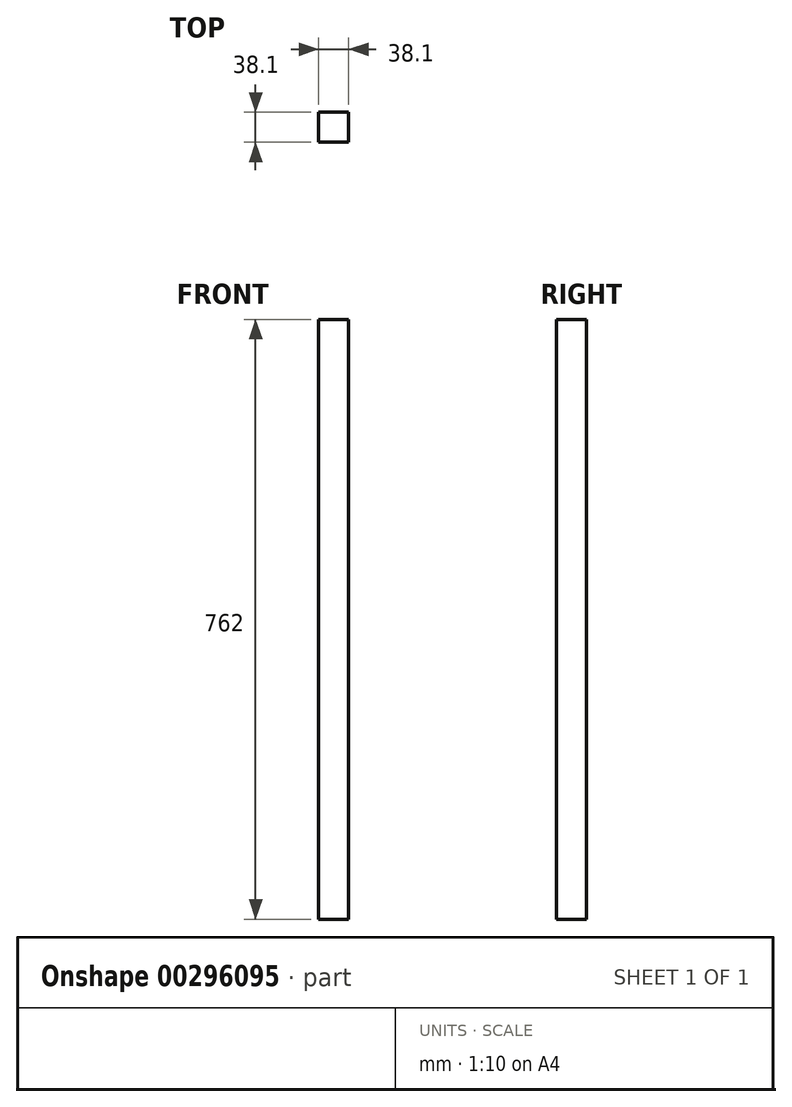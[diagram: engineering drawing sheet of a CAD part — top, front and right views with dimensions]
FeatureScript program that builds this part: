
annotation { "Feature Type Name" : "Feature", "Feature Type Description" : "" }
export const myFeature = defineFeature(function(context is Context, id is Id, definition is map)
    precondition{}
    {
        {
            var Q0;
            Q0=qCreatedBy(makeId("Front.planeOp"),FACE);
            var sketch = newSketch(context, id + "F0", { "sketchPlane" : qUnion([Q0])});
            skLineSegment(sketch, "E0.bottom", {"start": v(19.05, 381) * mm, "end": v(-19.05, 381) * mm});
            skLineSegment(sketch, "E0.top", {"start": v(19.05, -381) * mm, "end": v(-19.05, -381) * mm});
            skLineSegment(sketch, "E0.left", {"start": v(19.05, 381) * mm, "end": v(19.05, -381) * mm});
            skLineSegment(sketch, "E0.right", {"start": v(-19.05, 381) * mm, "end": v(-19.05, -381) * mm});
            skPoint(sketch, "E0.middle", {"position": v(0, 0) * mm});
            skSolve(sketch);
        }
        {
            var Q0;
            Q0=makeQuery(id+"F0.imprint","IMPRINT",FACE,{"disambiguationData":[TD([[makeQuery(id+"F0.imprint","IMPRINT",EDGE,{"derivedFrom":sQuery(id+"F0.wireOp",EDGE,"E0.bottom")}),1.0]])]});
            extrude(context, id + "F1", {"entities" : qUnion([Q0]), "depth" : 38.1 * mm});
        }
    });
